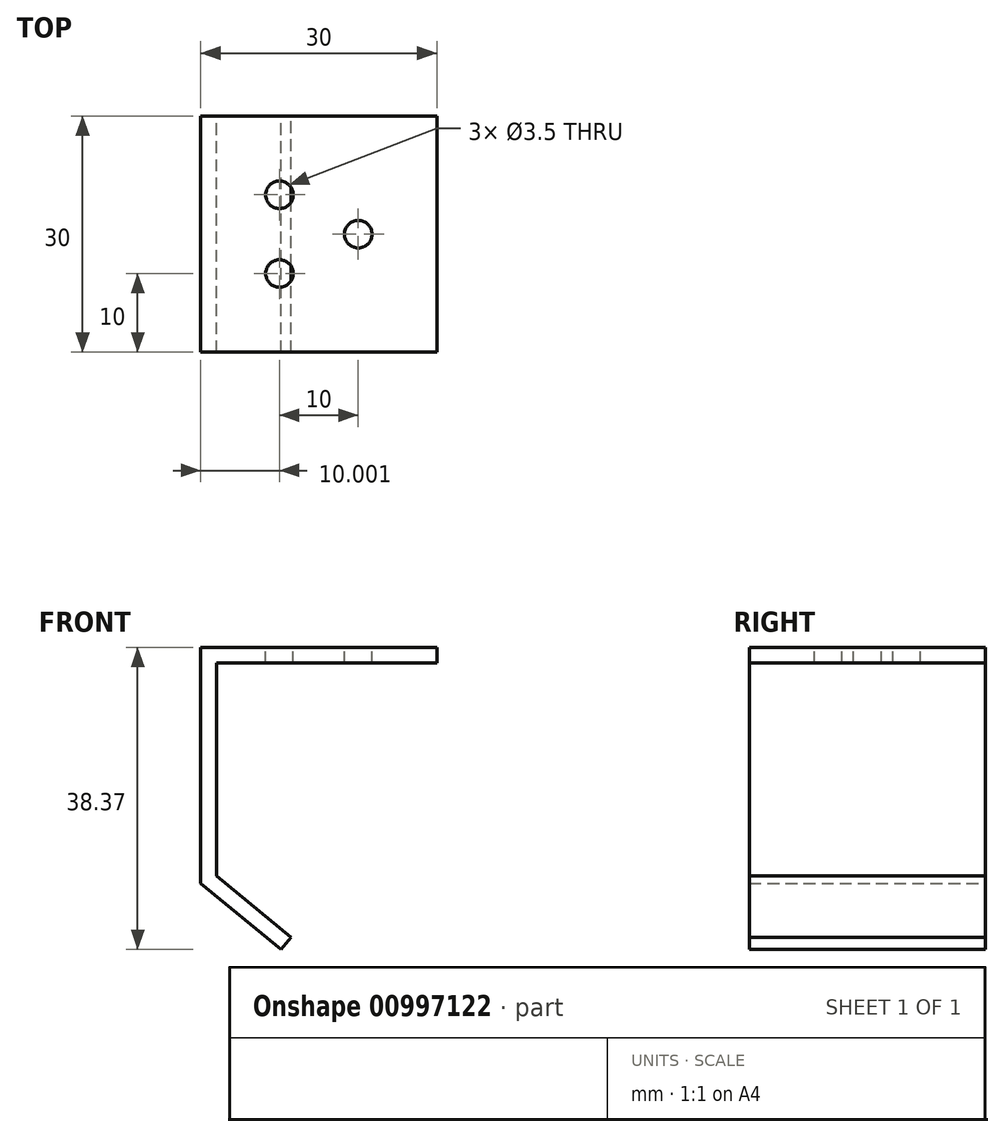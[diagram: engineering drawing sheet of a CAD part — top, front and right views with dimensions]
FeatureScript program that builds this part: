
annotation { "Feature Type Name" : "Feature", "Feature Type Description" : "" }
export const myFeature = defineFeature(function(context is Context, id is Id, definition is map)
    precondition{}
    {
        {
            var Q0;
            Q0=qCreatedBy(makeId("Front.planeOp"),FACE);
            var sketch = newSketch(context, id + "F0", { "sketchPlane" : qUnion([Q0])});
            skLineSegment(sketch, "E0", {"start": v(-2.96, 12.36) * mm, "end": v(27.04, 12.36) * mm});
            skLineSegment(sketch, "E1", {"start": v(27.04, 12.36) * mm, "end": v(27.04, 10.36) * mm});
            skLineSegment(sketch, "E2", {"start": v(27.04, 10.36) * mm, "end": v(-0.96, 10.36) * mm});
            skLineSegment(sketch, "E3", {"start": v(-0.96, 10.36) * mm, "end": v(-0.96, -16.69) * mm});
            skLineSegment(sketch, "E4", {"start": v(-0.96, -16.69) * mm, "end": v(8.5, -24.46) * mm});
            skLineSegment(sketch, "E5", {"start": v(8.5, -24.46) * mm, "end": v(7.23, -26) * mm});
            skLineSegment(sketch, "E6", {"start": v(7.23, -26) * mm, "end": v(-2.96, -17.64) * mm});
            skLineSegment(sketch, "E7", {"start": v(-2.96, -17.64) * mm, "end": v(-2.96, 12.36) * mm});
            skSolve(sketch);
        }
        {
            var Q0;
            Q0 = qSketchRegion(id + "F0", true);
            extrude(context, id + "F1", {"entities" : qUnion([Q0]), "depth" : 30 * mm, "offsetDistance" : 25 * mm});
        }
        {
            var Q0;
            Q0=makeQuery(id+"F1.opExtrude","SWEPT_FACE",FACE,{"disambiguationData":[OSD([sQuery(id+"F0.wireOp",EDGE,"E0")])]});
            var sketch = newSketch(context, id + "F2", { "sketchPlane" : qUnion([Q0])});
            skPoint(sketch, "E8", {"position": v(7.04, -10) * mm});
            skPoint(sketch, "E9", {"position": v(7.04, -20) * mm});
            skPoint(sketch, "E10", {"position": v(17.04, -15) * mm});
            skSolve(sketch);
        }
        {
            var Q0;
            Q0=sQuery(id+"F2.wireOp",VERTEX,"E8");
            var Q1;
            Q1=sQuery(id+"F2.wireOp",VERTEX,"E10");
            var Q2;
            Q2=sQuery(id+"F2.wireOp",VERTEX,"E9");
            var Q3;
            Q3=makeQuery(id+"F1.opExtrude","SWEPT_BODY",BODY,{"disambiguationData":[OSD([sQuery(id+"F0.wireOp",EDGE,"E0"),sQuery(id+"F0.wireOp",EDGE,"E1"),sQuery(id+"F0.wireOp",EDGE,"E2"),sQuery(id+"F0.wireOp",EDGE,"E3"),sQuery(id+"F0.wireOp",EDGE,"E4"),sQuery(id+"F0.wireOp",EDGE,"E5"),sQuery(id+"F0.wireOp",EDGE,"E6"),sQuery(id+"F0.wireOp",EDGE,"E7")])]});
            hole(context, id + "F3", {"style" : HoleStyle.SIMPLE, "endStyle" : HoleEndStyle.BLIND, "holeDiameter" : 3.5 * mm, "majorDiameter" : 5 * mm, "holeDepth" : 5 * mm, "isTappedThrough" : true, "tappedDepth" : 12 * mm, "tapClearance" : 3, "locations" : qUnion([Q0, Q1, Q2]), "scope" : qUnion([Q3])});
        }
    });
